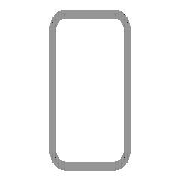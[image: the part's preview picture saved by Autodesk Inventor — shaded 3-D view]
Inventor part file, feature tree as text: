
AUTODESK INVENTOR PART (.ipt)
format: ipt  version: 2025 (Build 290162010, 162A)  size: 134,656 bytes
history: native  units: mm (DEFAULTED — no unit token found)
features: other x4, sketch x1, plane x1
ambient origin geometry x8: Origin, YZ Plane, XZ Plane, XY Plane, X Axis, Y Axis, Z Axis, Center Point
bodies: Solid1 (feature_tree), Body (feature_tree)
feature tree (6):
  parser-record x1  (decoder bookkeeping rows leaked as tree rows — omitted from the tree; the rows remain in map.json)
  other  "Driven Length"
  other  "Start Plane"
  other  "End Plane"
  sketch  "Sketch3"  dims[d3=2790.0mm d4=0.0mm d7=6.0mm d9=40.0mm d11=80.0mm d12=3.0mm d13=80.0mm d14=2870.0mm d15=20.0mm d16=40.0mm d17=90.0deg d18=2790.0mm]
  plane  "Work Plane3"
